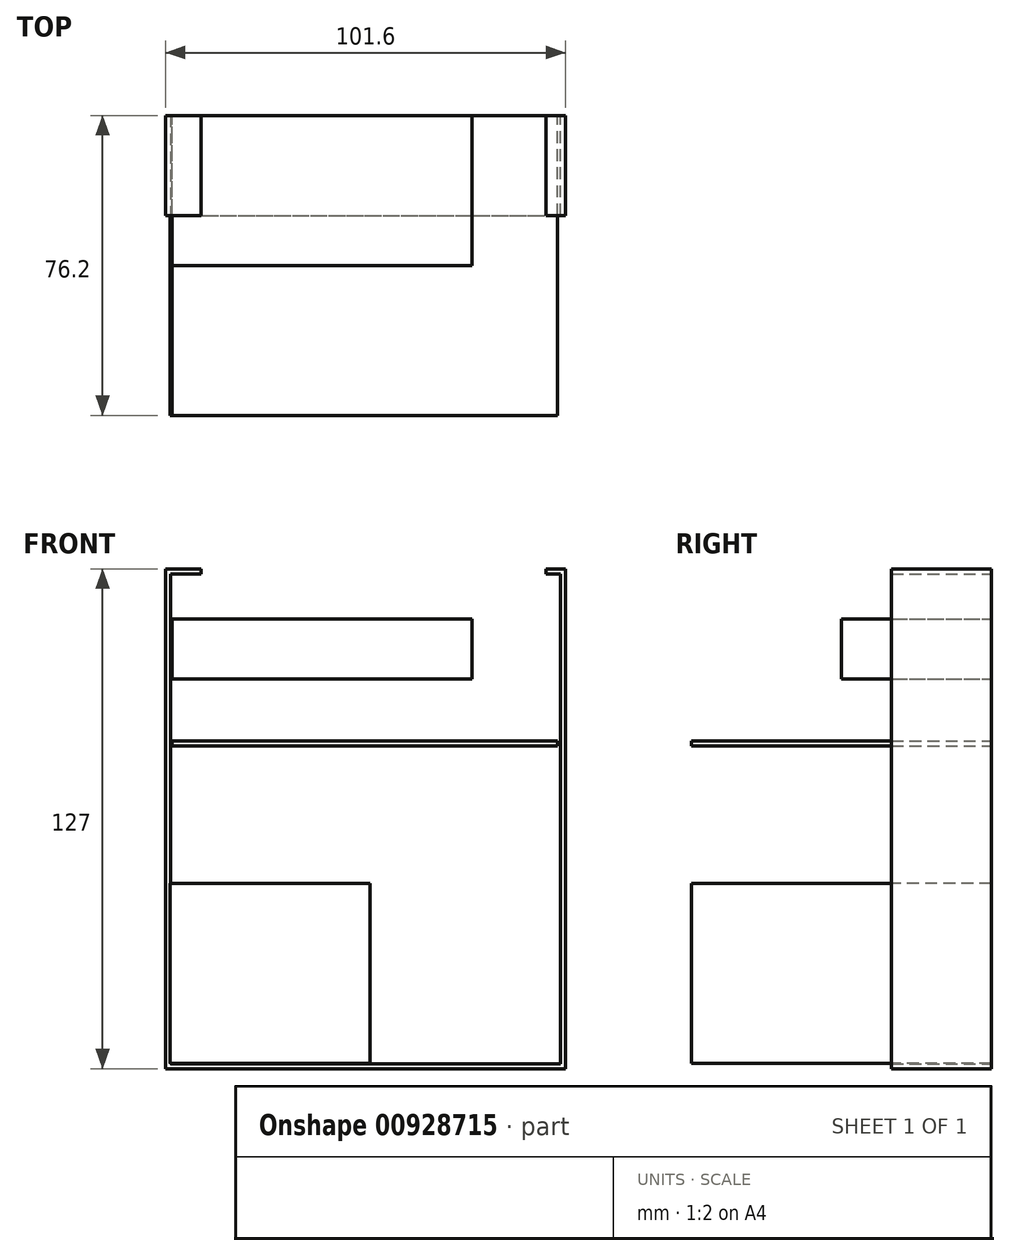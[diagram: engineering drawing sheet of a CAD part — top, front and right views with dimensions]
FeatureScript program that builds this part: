
annotation { "Feature Type Name" : "Feature", "Feature Type Description" : "" }
export const myFeature = defineFeature(function(context is Context, id is Id, definition is map)
    precondition{}
    {
        {
            var Q0;
            Q0=qCreatedBy(makeId("Front.planeOp"),FACE);
            var sketch = newSketch(context, id + "F0", { "sketchPlane" : qUnion([Q0])});
            skLineSegment(sketch, "E0.bottom", {"start": v(-56.67, 62.86) * mm, "end": v(-47.64, 62.86) * mm});
            skLineSegment(sketch, "E0.top", {"start": v(-56.67, -64.14) * mm, "end": v(44.93, -64.14) * mm});
            skLineSegment(sketch, "E0.left", {"start": v(-56.67, 62.86) * mm, "end": v(-56.67, -64.14) * mm});
            skLineSegment(sketch, "E0.right", {"start": v(44.93, 62.86) * mm, "end": v(44.93, -64.14) * mm});
            skLineSegment(sketch, "E1.0", {"start": v(-55.4, 61.59) * mm, "end": v(-47.64, 61.59) * mm});
            skLineSegment(sketch, "E1.1", {"start": v(-55.4, 61.59) * mm, "end": v(-55.4, -62.87) * mm});
            skLineSegment(sketch, "E1.2", {"start": v(-55.4, -62.87) * mm, "end": v(43.66, -62.87) * mm});
            skLineSegment(sketch, "E1.3", {"start": v(43.66, 61.59) * mm, "end": v(43.66, -62.87) * mm});
            skLineSegment(sketch, "E2.left", {"start": v(-47.64, 62.86) * mm, "end": v(-47.64, 61.59) * mm});
            skLineSegment(sketch, "E2.right", {"start": v(39.92, 62.86) * mm, "end": v(39.92, 61.59) * mm});
            skLineSegment(sketch, "E3.trimOffspring", {"start": v(39.92, 61.59) * mm, "end": v(43.66, 61.59) * mm});
            skLineSegment(sketch, "E4.trimOffspring", {"start": v(39.92, 62.86) * mm, "end": v(44.93, 62.86) * mm});
            skSolve(sketch);
        }
        {
            var Q0;
            Q0=qCreatedBy(makeId("Front.planeOp"),FACE);
            var sketch = newSketch(context, id + "F1", { "sketchPlane" : qUnion([Q0])});
            skLineSegment(sketch, "E5.bottom", {"start": v(-55.49, -62.8) * mm, "end": v(-4.69, -62.8) * mm});
            skLineSegment(sketch, "E5.top", {"start": v(-55.49, -17.09) * mm, "end": v(-4.69, -17.09) * mm});
            skLineSegment(sketch, "E5.left", {"start": v(-55.49, -62.8) * mm, "end": v(-55.49, -17.09) * mm});
            skLineSegment(sketch, "E5.right", {"start": v(-4.69, -62.8) * mm, "end": v(-4.69, -17.09) * mm});
            skSolve(sketch);
        }
        {
            var Q0;
            Q0 = qSketchRegion(id + "F0", true);
            extrude(context, id + "F2", {"entities" : qUnion([Q0]), "depth" : 25.4 * mm, "offsetDistance" : 25.4 * mm});
        }
        {
            var Q0;
            Q0 = qSketchRegion(id + "F1", true);
            extrude(context, id + "F3", {"entities" : qUnion([Q0]), "operationType" : NewBodyOperationType.ADD, "depth" : 76.2 * mm, "offsetDistance" : 25.4 * mm});
        }
        {
            var Q0;
            Q0=qCreatedBy(makeId("Front.planeOp"),FACE);
            var sketch = newSketch(context, id + "F4", { "sketchPlane" : qUnion([Q0])});
            skLineSegment(sketch, "E6.bottom", {"start": v(-54.97, 19.15) * mm, "end": v(42.92, 19.15) * mm});
            skLineSegment(sketch, "E6.top", {"start": v(-54.97, 17.88) * mm, "end": v(42.92, 17.88) * mm});
            skLineSegment(sketch, "E6.left", {"start": v(-54.97, 19.15) * mm, "end": v(-54.97, 17.88) * mm});
            skLineSegment(sketch, "E6.right", {"start": v(42.92, 19.15) * mm, "end": v(42.92, 17.88) * mm});
            skSolve(sketch);
        }
        {
            var Q0;
            Q0 = qSketchRegion(id + "F4", true);
            extrude(context, id + "F5", {"entities" : qUnion([Q0]), "depth" : 76.2 * mm, "offsetDistance" : 25.4 * mm});
        }
        {
            var Q0;
            Q0=qCreatedBy(makeId("Front.planeOp"),FACE);
            var sketch = newSketch(context, id + "F6", { "sketchPlane" : qUnion([Q0])});
            skLineSegment(sketch, "E7.bottom", {"start": v(-55.08, 50.16) * mm, "end": v(21.12, 50.16) * mm});
            skLineSegment(sketch, "E7.top", {"start": v(-55.08, 34.92) * mm, "end": v(21.12, 34.92) * mm});
            skLineSegment(sketch, "E7.left", {"start": v(-55.08, 50.16) * mm, "end": v(-55.08, 34.92) * mm});
            skLineSegment(sketch, "E7.right", {"start": v(21.12, 50.16) * mm, "end": v(21.12, 34.92) * mm});
            skSolve(sketch);
        }
        {
            var Q0;
            Q0 = qSketchRegion(id + "F6", true);
            extrude(context, id + "F7", {"entities" : qUnion([Q0]), "depth" : 38.1 * mm, "offsetDistance" : 25.4 * mm});
        }
    });
